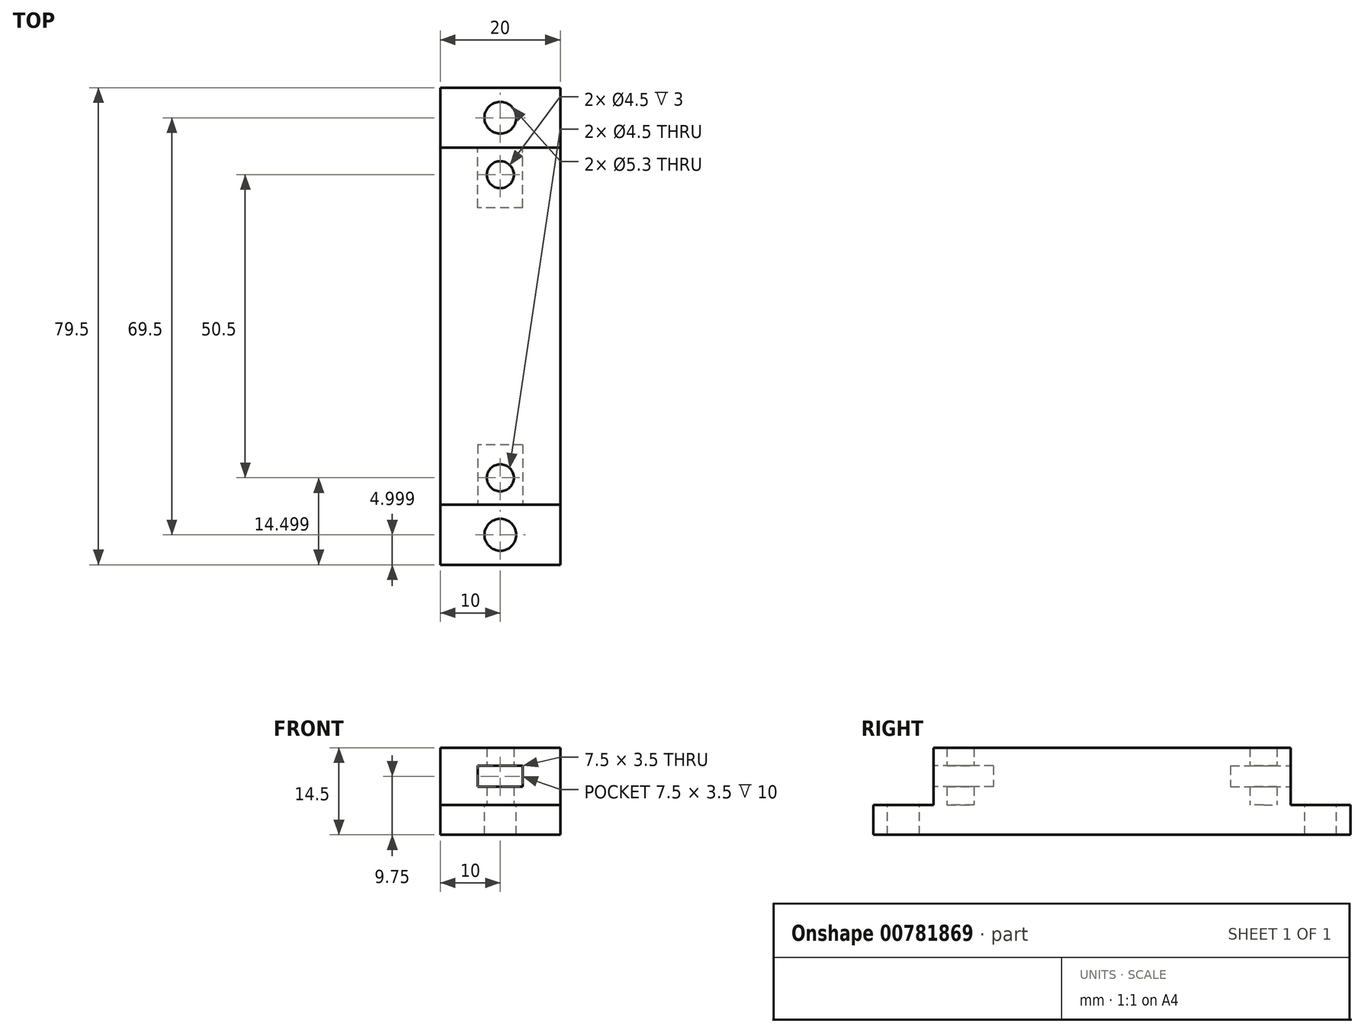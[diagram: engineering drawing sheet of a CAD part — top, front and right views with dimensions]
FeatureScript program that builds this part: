
annotation { "Feature Type Name" : "Feature", "Feature Type Description" : "" }
export const myFeature = defineFeature(function(context is Context, id is Id, definition is map)
    precondition{}
    {
        {
            var Q0;
            Q0=qCreatedBy(makeId("Top.planeOp"),FACE);
            var sketch = newSketch(context, id + "F0", { "sketchPlane" : qUnion([Q0])});
            skLineSegment(sketch, "E0.bottom", {"start": v(-20, 28.69) * mm, "end": v(0, 28.69) * mm});
            skLineSegment(sketch, "E0.top", {"start": v(-20, -30.81) * mm, "end": v(0, -30.81) * mm});
            skLineSegment(sketch, "E0.left", {"start": v(-20, 28.69) * mm, "end": v(-20, -30.81) * mm});
            skLineSegment(sketch, "E0.right", {"start": v(0, 28.69) * mm, "end": v(0, -30.81) * mm});
            skCircle(sketch, "E1", {"center": v(-10, 24.19) * mm, "radius": 2.25 * mm});
            skCircle(sketch, "E2", {"center": v(-10, -26.31) * mm, "radius": 2.25 * mm});
            skSolve(sketch);
        }
        {
            var Q0;
            Q0=makeQuery(id+"F0.imprint","IMPRINT",FACE,{"disambiguationData":[TD([[makeQuery(id+"F0.imprint","IMPRINT",EDGE,{"derivedFrom":sQuery(id+"F0.wireOp",EDGE,"E0.bottom")}),-1.0]])]});
            extrude(context, id + "F1", {"entities" : qUnion([Q0]), "depth" : 9.5 * mm, "offsetDistance" : 25 * mm});
        }
        {
            var Q0;
            Q0=makeQuery(id+"F1.opExtrude","SWEPT_FACE",FACE,{"disambiguationData":[OSD([sQuery(id+"F0.wireOp",EDGE,"E0.bottom")])]});
            var sketch = newSketch(context, id + "F2", { "sketchPlane" : qUnion([Q0])});
            skLineSegment(sketch, "E3.bottom", {"start": v(6.25, 6.5) * mm, "end": v(13.75, 6.5) * mm});
            skLineSegment(sketch, "E3.top", {"start": v(6.25, 3) * mm, "end": v(13.75, 3) * mm});
            skLineSegment(sketch, "E3.left", {"start": v(6.25, 6.5) * mm, "end": v(6.25, 3) * mm});
            skLineSegment(sketch, "E3.right", {"start": v(13.75, 6.5) * mm, "end": v(13.75, 3) * mm});
            skLineSegment(sketch, "E4", {"start": v(10, 9.72) * mm, "end": v(10, 0) * mm, "construction": true});
            skPoint(sketch, "E4.startSnap0", {"position": v(10, 9.5) * mm});
            skLineSegment(sketch, "E5", {"start": v(20, 4.75) * mm, "end": v(0, 4.75) * mm, "construction": true});
            skSolve(sketch);
        }
        {
            var Q0;
            Q0 = qSketchRegion(id + "F2", true);
            extrude(context, id + "F3", {"entities" : qUnion([Q0]), "operationType" : NewBodyOperationType.REMOVE, "oppositeDirection" : true, "depth" : 10 * mm, "offsetDistance" : 25 * mm});
        }
        {
            var Q0;
            Q0=makeQuery(id+"F1.opExtrude","SWEPT_FACE",FACE,{"disambiguationData":[OSD([sQuery(id+"F0.wireOp",EDGE,"E0.top")])]});
            var sketch = newSketch(context, id + "F4", { "sketchPlane" : qUnion([Q0])});
            skLineSegment(sketch, "E6.0", {"start": v(-6.25, 6.5) * mm, "end": v(-13.75, 6.5) * mm});
            skLineSegment(sketch, "E6.1", {"start": v(-13.75, 6.5) * mm, "end": v(-13.75, 3) * mm});
            skLineSegment(sketch, "E6.2", {"start": v(-6.25, 3) * mm, "end": v(-13.75, 3) * mm});
            skLineSegment(sketch, "E6.3", {"start": v(-6.25, 6.5) * mm, "end": v(-6.25, 3) * mm});
            skSolve(sketch);
        }
        {
            var Q0;
            Q0 = qSketchRegion(id + "F4", true);
            extrude(context, id + "F5", {"entities" : qUnion([Q0]), "operationType" : NewBodyOperationType.REMOVE, "oppositeDirection" : true, "depth" : 10 * mm, "offsetDistance" : 25 * mm});
        }
        {
            var Q0;
            Q0=makeQuery(id+"F1.opExtrude","CAP_FACE",FACE,{"disambiguationData":[OSD([sQuery(id+"F0.wireOp",EDGE,"E0.bottom"),sQuery(id+"F0.wireOp",EDGE,"E0.top"),sQuery(id+"F0.wireOp",EDGE,"E0.left"),sQuery(id+"F0.wireOp",EDGE,"E0.right"),sQuery(id+"F0.wireOp",EDGE,"E1"),sQuery(id+"F0.wireOp",EDGE,"E2")])],"isStart":true});
            var sketch = newSketch(context, id + "F6", { "sketchPlane" : qUnion([Q0])});
            skLineSegment(sketch, "E7.0", {"start": v(-20, 40.81) * mm, "end": v(0, 40.81) * mm});
            skLineSegment(sketch, "E8.0", {"start": v(-20, -38.69) * mm, "end": v(0, -38.69) * mm});
            skLineSegment(sketch, "E9", {"start": v(-20, -38.69) * mm, "end": v(-20, 40.81) * mm});
            skLineSegment(sketch, "E10", {"start": v(0, -38.69) * mm, "end": v(0, 40.81) * mm});
            skSolve(sketch);
        }
        {
            var Q0;
            Q0 = qSketchRegion(id + "F6", true);
            extrude(context, id + "F7", {"entities" : qUnion([Q0]), "operationType" : NewBodyOperationType.ADD, "depth" : 5 * mm, "offsetDistance" : 25 * mm});
        }
        {
            var Q0;
            {var subQ0=sQuery(id+"F6.wireOp",EDGE,"E8.0");var subQ1=sQuery(id+"F6.wireOp",EDGE,"E9");var subQ2=sQuery(id+"F6.wireOp",EDGE,"E10");Q0=makeQuery(id+"F7.boolean.opBoolean","SPLIT",FACE,{"disambiguationData":[TD([makeQuery(id+"F1.opExtrude","SWEPT_FACE",FACE,{"disambiguationData":[OSD([sQuery(id+"F0.wireOp",EDGE,"E0.bottom")])]})])],"derivedFrom":makeQuery(id+"F7.opExtrude","CAP_FACE",FACE,{"disambiguationData":[OSD([sQuery(id+"F6.wireOp",EDGE,"E7.0"),subQ0,subQ1,subQ2])],"isStart":true})});}
            var sketch = newSketch(context, id + "F8", { "sketchPlane" : qUnion([Q0])});
            skCircle(sketch, "E11", {"center": v(-10, 33.69) * mm, "radius": 2.65 * mm});
            skLineSegment(sketch, "E12", {"start": v(-10, 38.69) * mm, "end": v(-10, -40.92) * mm, "construction": true});
            skLineSegment(sketch, "E13", {"start": v(0, 33.69) * mm, "end": v(-20, 33.69) * mm, "construction": true});
            skCircle(sketch, "E14", {"center": v(-10, -35.81) * mm, "radius": 2.65 * mm});
            skSolve(sketch);
        }
        {
            var Q0;
            Q0=makeQuery(id+"F8.imprint","IMPRINT",FACE,{"disambiguationData":[TD([[makeQuery(id+"F8.imprint","IMPRINT",EDGE,{"derivedFrom":sQuery(id+"F8.wireOp",EDGE,"E11")}),1.0]])]});
            var Q1;
            Q1=makeQuery(id+"F8.imprint","IMPRINT",FACE,{"disambiguationData":[TD([[makeQuery(id+"F8.imprint","IMPRINT",EDGE,{"derivedFrom":sQuery(id+"F8.wireOp",EDGE,"E14")}),1.0]])]});
            extrude(context, id + "F9", {"entities" : qUnion([Q0, Q1]), "operationType" : NewBodyOperationType.REMOVE, "oppositeDirection" : true, "depth" : 25 * mm, "offsetDistance" : 25 * mm});
        }
    });
